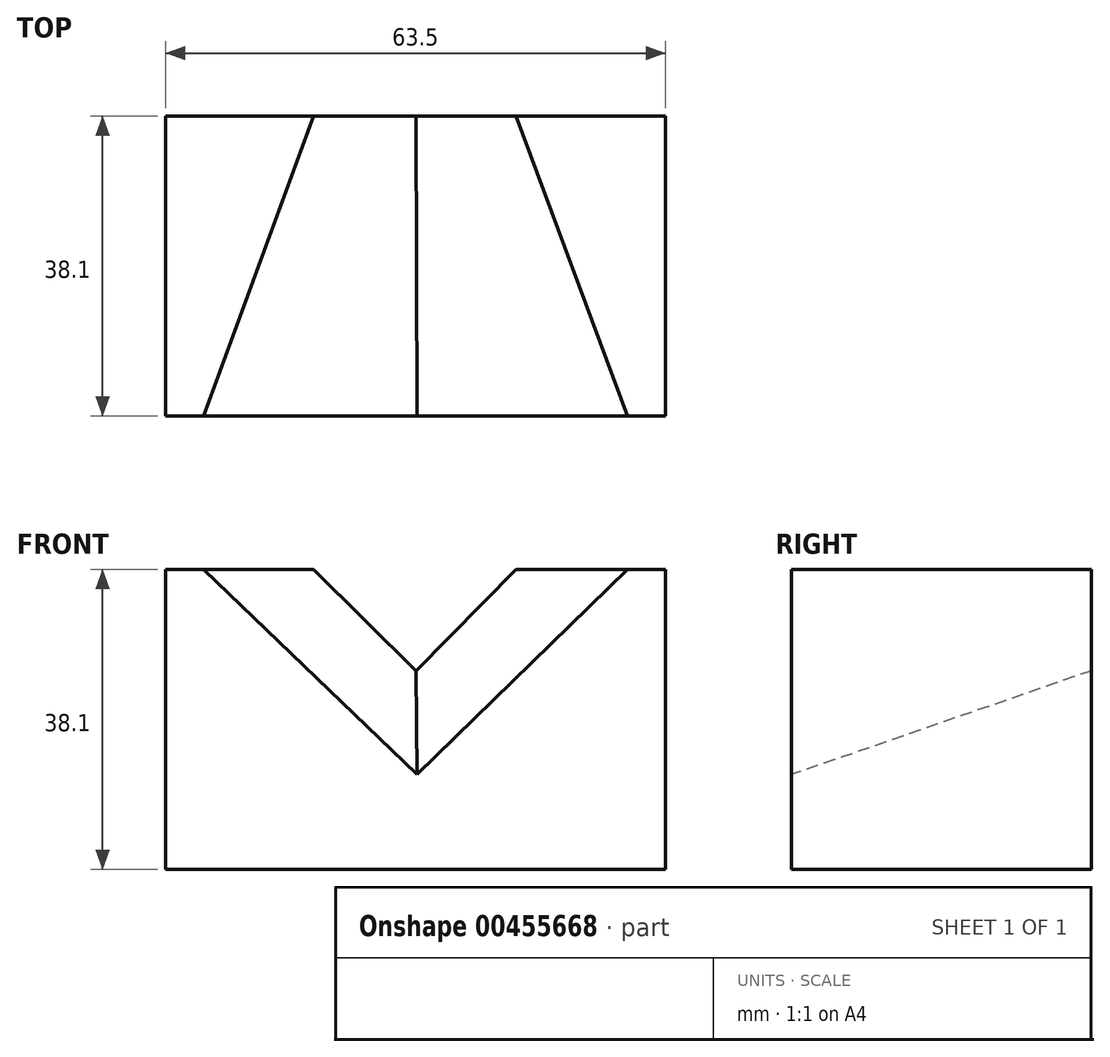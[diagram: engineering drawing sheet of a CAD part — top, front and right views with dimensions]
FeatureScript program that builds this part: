
annotation { "Feature Type Name" : "Feature", "Feature Type Description" : "" }
export const myFeature = defineFeature(function(context is Context, id is Id, definition is map)
    precondition{}
    {
        {
            var Q0;
            Q0=qCreatedBy(makeId("Front.planeOp"),FACE);
            var sketch = newSketch(context, id + "F0", { "sketchPlane" : qUnion([Q0])});
            skLineSegment(sketch, "E0.bottom", {"start": v(0, 0) * mm, "end": v(63.5, 0) * mm});
            skLineSegment(sketch, "E0.top", {"start": v(0, 38.1) * mm, "end": v(63.5, 38.1) * mm});
            skLineSegment(sketch, "E0.left", {"start": v(0, 0) * mm, "end": v(0, 38.1) * mm});
            skLineSegment(sketch, "E0.right", {"start": v(63.5, 0) * mm, "end": v(63.5, 38.1) * mm});
            skSolve(sketch);
        }
        {
            var Q0;
            Q0=makeQuery(id+"F0.imprint","IMPRINT",FACE,{"disambiguationData":[TD([[makeQuery(id+"F0.imprint","IMPRINT",EDGE,{"derivedFrom":sQuery(id+"F0.wireOp",EDGE,"E0.bottom")}),1.0]])]});
            extrude(context, id + "F1", {"entities" : qUnion([Q0]), "depth" : 38.1 * mm});
        }
        {
            var Q0;
            Q0=makeQuery(id+"F1.opExtrude","CAP_FACE",FACE,{"disambiguationData":[OSD([sQuery(id+"F0.wireOp",EDGE,"E0.bottom"),sQuery(id+"F0.wireOp",EDGE,"E0.top"),sQuery(id+"F0.wireOp",EDGE,"E0.left"),sQuery(id+"F0.wireOp",EDGE,"E0.right")])],"isStart":false});
            var sketch = newSketch(context, id + "F2", { "sketchPlane" : qUnion([Q0])});
            skLineSegment(sketch, "E1", {"start": v(0, 38.1) * mm, "end": v(4.84, 38.1) * mm});
            skLineSegment(sketch, "E2", {"start": v(4.84, 38.1) * mm, "end": v(58.65, 38.1) * mm});
            skLineSegment(sketch, "E3", {"start": v(58.65, 38.1) * mm, "end": v(63.5, 38.1) * mm});
            skLineSegment(sketch, "E4", {"start": v(4.84, 38.1) * mm, "end": v(31.92, 12.04) * mm});
            skLineSegment(sketch, "E5", {"start": v(31.92, 12.04) * mm, "end": v(58.65, 38.1) * mm});
            skSolve(sketch);
        }
        {
            var Q0;
            Q0=makeQuery(id+"F1.opExtrude","CAP_FACE",FACE,{"disambiguationData":[OSD([sQuery(id+"F0.wireOp",EDGE,"E0.bottom"),sQuery(id+"F0.wireOp",EDGE,"E0.top"),sQuery(id+"F0.wireOp",EDGE,"E0.left"),sQuery(id+"F0.wireOp",EDGE,"E0.right")])],"isStart":true});
            var sketch = newSketch(context, id + "F3", { "sketchPlane" : qUnion([Q0])});
            skLineSegment(sketch, "E6", {"start": v(-44.5, 38.1) * mm, "end": v(-31.81, 25.25) * mm});
            skLineSegment(sketch, "E7", {"start": v(-31.81, 25.25) * mm, "end": v(-18.79, 38.1) * mm});
            skLineSegment(sketch, "E8", {"start": v(-18.79, 38.1) * mm, "end": v(-44.5, 38.1) * mm});
            skSolve(sketch);
        }
        {
            var Q1;
            Q1=makeQuery(id+"F3.imprint","IMPRINT",FACE,{"disambiguationData":[TD([[makeQuery(id+"F3.imprint","IMPRINT",EDGE,{"derivedFrom":sQuery(id+"F3.wireOp",EDGE,"E6")}),1.0]])]});
            var Q2;
            Q2=makeQuery(id+"F2.imprint","IMPRINT",FACE,{"disambiguationData":[TD([[makeQuery(id+"F2.imprint","IMPRINT",EDGE,{"derivedFrom":sQuery(id+"F2.wireOp",EDGE,"E2")}),-1.0]])]});
            loft(context, id + "F4", {"operationType" : NewBodyOperationType.REMOVE, "sheetProfilesArray" : [{ "sheetProfileEntities" : qUnion([Q1]) }, { "sheetProfileEntities" : qUnion([Q2]) }]});
        }
    });
